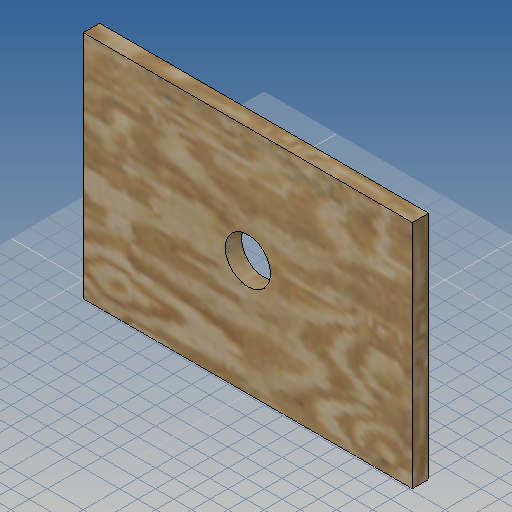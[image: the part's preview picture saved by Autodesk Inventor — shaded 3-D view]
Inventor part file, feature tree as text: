
AUTODESK INVENTOR PART (.ipt)
format: ipt  version: 2019 (Build 230136000, 136)  size: 306,688 bytes
history: native  units: mm
features: extrude x2, sketch x2, other x1
ambient origin geometry x8: Origin, YZ Plane, XZ Plane, XY Plane, X Axis, Y Axis, Z Axis, Center Point
bodies: Volumenkörper1 (feature_tree)
feature tree (5):
  other  "<userpath>\OneDrive\Dokumente\Inventor\Absauganlage\Absauganlage_Params.xlsx"
  extrude  "Extrusion1"  Depth=364.0mm
  extrude  "Extrusion2"  TaperAngle=0.0deg  [1 undecoded]
  sketch  "Skizze1"  dims[d0=255.0mm d1=364.0mm]
  sketch  "Skizze2"  dims[d2=18.0mm d3=0.0mm d4=50.0mm d6=10.0mm d7=0.0mm]
note: 1 required parameter value undecoded (feature->parameter linkage not recoverable at this tier; creation-order binding heuristic only, values carry confidence <= 0.55)
